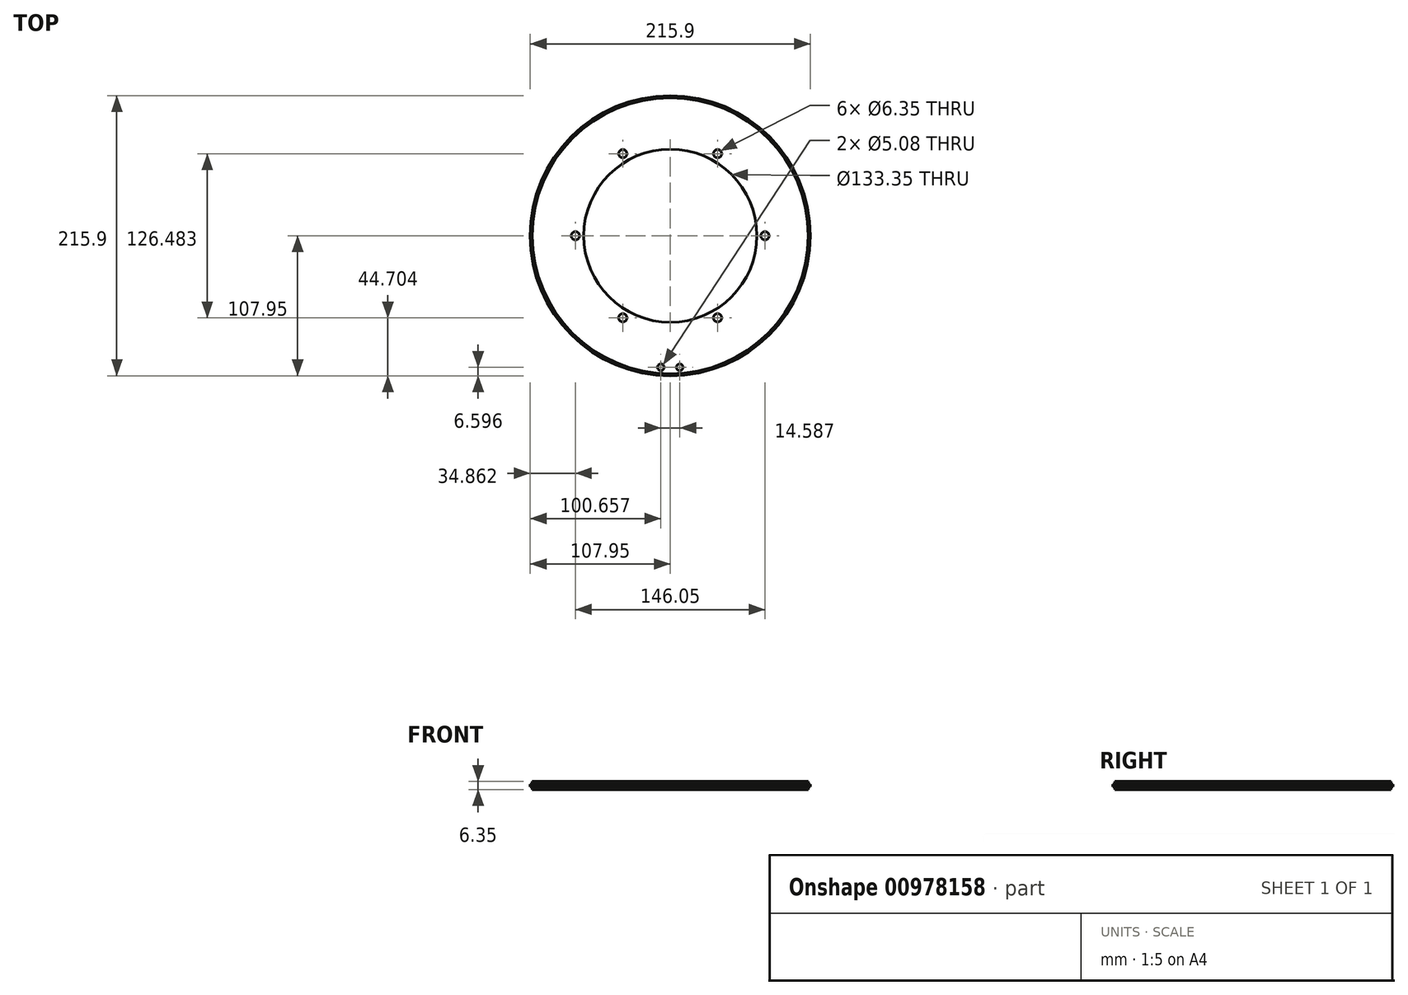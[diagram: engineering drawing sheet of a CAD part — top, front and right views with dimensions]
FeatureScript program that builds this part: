
annotation { "Feature Type Name" : "Feature", "Feature Type Description" : "" }
export const myFeature = defineFeature(function(context is Context, id is Id, definition is map)
    precondition{}
    {
        {
            var Q0;
            Q0=qCreatedBy(makeId("Top.planeOp"),FACE);
            var sketch = newSketch(context, id + "F0", { "sketchPlane" : qUnion([Q0])});
            skCircle(sketch, "E0", {"center": v(0, 0) * mm, "radius": 107.95 * mm});
            skCircle(sketch, "E1", {"center": v(0, 0) * mm, "radius": 106.35 * mm});
            skSolve(sketch);
        }
        {
            var Q0;
            Q0=makeQuery(id+"F0.imprint","IMPRINT",FACE,{"disambiguationData":[TD([[makeQuery(id+"F0.imprint","IMPRINT",EDGE,{"derivedFrom":sQuery(id+"F0.wireOp",EDGE,"E1")}),1.0]])]});
            extrude(context, id + "F1", {"entities" : qUnion([Q0]), "depth" : 2.12 * mm, "offsetDistance" : 25.4 * mm});
        }
        {
            var Q0;
            Q0=qSketchRegion(id+"F0",true);
            var Q1;
            Q1=makeQuery(id+"F1.opExtrude","CAP_FACE",FACE,{"disambiguationData":[OSD([sQuery(id+"F0.wireOp",EDGE,"E1")])],"isStart":true});
            extrude(context, id + "F2", {"entities" : qUnion([Q0, Q1]), "operationType" : NewBodyOperationType.ADD, "oppositeDirection" : true, "depth" : 2.12 * mm, "offsetDistance" : 25.4 * mm});
        }
        {
            var Q0;
            Q0=makeQuery(id+"F0.imprint","IMPRINT",FACE,{"disambiguationData":[TD([[makeQuery(id+"F0.imprint","IMPRINT",EDGE,{"derivedFrom":sQuery(id+"F0.wireOp",EDGE,"E1")}),1.0]])]});
            extrude(context, id + "F3", {"entities" : qUnion([Q0]), "operationType" : NewBodyOperationType.ADD, "oppositeDirection" : true, "depth" : 4.23 * mm, "offsetDistance" : 25.4 * mm});
        }
        {
            var Q0;
            Q0=makeQuery(id+"F1.opExtrude","CAP_FACE",FACE,{"disambiguationData":[OSD([sQuery(id+"F0.wireOp",EDGE,"E1")])],"isStart":false});
            var sketch = newSketch(context, id + "F4", { "sketchPlane" : qUnion([Q0])});
            skCircle(sketch, "E2", {"center": v(0, 0) * mm, "radius": 66.68 * mm});
            skSolve(sketch);
        }
        {
            var Q0;
            Q0=qSketchRegion(id+"F4",true);
            extrude(context, id + "F5", {"entities" : qUnion([Q0]), "operationType" : NewBodyOperationType.REMOVE, "endBound" : BoundingType.THROUGH_ALL, "oppositeDirection" : true, "depth" : 25.4 * mm, "offsetDistance" : 25.4 * mm});
        }
        {
            var Q0;
            Q0=makeQuery(id+"F1.opExtrude","CAP_FACE",FACE,{"disambiguationData":[OSD([sQuery(id+"F0.wireOp",EDGE,"E1")])],"isStart":false});
            var sketch = newSketch(context, id + "F6", { "sketchPlane" : qUnion([Q0])});
            skCircle(sketch, "E3", {"center": v(-0.06, 0) * mm, "radius": 79.4 * mm});
            skCircle(sketch, "E4", {"center": v(-0.06, 0) * mm, "radius": 77.76 * mm});
            skCircle(sketch, "E5.0", {"center": v(-73.09, 0) * mm, "radius": 3.17 * mm});
            skCircle(sketch, "E6.0", {"center": v(-36.58, 63.24) * mm, "radius": 3.17 * mm});
            skCircle(sketch, "E7.0", {"center": v(36.45, 63.24) * mm, "radius": 3.17 * mm});
            skCircle(sketch, "E8.0", {"center": v(72.96, 0) * mm, "radius": 3.17 * mm});
            skCircle(sketch, "E9.0", {"center": v(36.45, -63.25) * mm, "radius": 3.17 * mm});
            skCircle(sketch, "E10.0", {"center": v(-36.58, -63.25) * mm, "radius": 3.17 * mm});
            skCircle(sketch, "E11.0", {"center": v(-7.36, -72.66) * mm, "radius": 2.54 * mm});
            skCircle(sketch, "E12.0", {"center": v(7.23, -72.66) * mm, "radius": 2.54 * mm});
            skCircle(sketch, "E13.0", {"center": v(-0.06, 0) * mm, "radius": 66.67 * mm});
            skSolve(sketch);
        }
        {
            var Q0;
            Q0=makeQuery(id+"F6.imprint","IMPRINT",FACE,{"disambiguationData":[TD([[makeQuery(id+"F6.imprint","IMPRINT",EDGE,{"derivedFrom":sQuery(id+"F6.wireOp",EDGE,"E5.0")}),1.0]])]});
            var Q1;
            Q1=makeQuery(id+"F6.imprint","IMPRINT",FACE,{"disambiguationData":[TD([[makeQuery(id+"F6.imprint","IMPRINT",EDGE,{"derivedFrom":sQuery(id+"F6.wireOp",EDGE,"E7.0")}),1.0]])]});
            var Q2;
            Q2=makeQuery(id+"F6.imprint","IMPRINT",FACE,{"disambiguationData":[TD([[makeQuery(id+"F6.imprint","IMPRINT",EDGE,{"derivedFrom":sQuery(id+"F6.wireOp",EDGE,"E8.0")}),1.0]])]});
            var Q3;
            Q3=makeQuery(id+"F6.imprint","IMPRINT",FACE,{"disambiguationData":[TD([[makeQuery(id+"F6.imprint","IMPRINT",EDGE,{"derivedFrom":sQuery(id+"F6.wireOp",EDGE,"E9.0")}),1.0]])]});
            var Q4;
            Q4=makeQuery(id+"F6.imprint","IMPRINT",FACE,{"disambiguationData":[TD([[makeQuery(id+"F6.imprint","IMPRINT",EDGE,{"derivedFrom":sQuery(id+"F6.wireOp",EDGE,"E10.0")}),1.0]])]});
            var Q5;
            Q5=makeQuery(id+"F6.imprint","IMPRINT",FACE,{"disambiguationData":[TD([[makeQuery(id+"F6.imprint","IMPRINT",EDGE,{"derivedFrom":sQuery(id+"F6.wireOp",EDGE,"E6.0")}),1.0]])]});
            extrude(context, id + "F7", {"entities" : qUnion([Q0, Q1, Q2, Q3, Q4, Q5]), "operationType" : NewBodyOperationType.REMOVE, "oppositeDirection" : true, "depth" : 25.4 * mm, "offsetDistance" : 25.4 * mm});
        }
        {
            var Q0;
            Q0=makeQuery(id+"F1.opExtrude","CAP_FACE",FACE,{"disambiguationData":[OSD([sQuery(id+"F0.wireOp",EDGE,"E1")])],"isStart":false});
            var sketch = newSketch(context, id + "F8", { "sketchPlane" : qUnion([Q0])});
            skCircle(sketch, "E14", {"center": v(-7.3, -101.35) * mm, "radius": 2.54 * mm});
            skCircle(sketch, "E15", {"center": v(7.3, -101.35) * mm, "radius": 2.54 * mm});
            skLineSegment(sketch, "E16", {"start": v(0, 0) * mm, "end": v(0, -109.25) * mm});
            skSolve(sketch);
        }
        {
            var Q0;
            Q0=makeQuery(id+"F8.imprint","IMPRINT",FACE,{"disambiguationData":[TD([[makeQuery(id+"F8.imprint","IMPRINT",EDGE,{"derivedFrom":sQuery(id+"F8.wireOp",EDGE,"E14")}),1.0]])]});
            var Q1;
            Q1=makeQuery(id+"F8.imprint","IMPRINT",FACE,{"disambiguationData":[TD([[makeQuery(id+"F8.imprint","IMPRINT",EDGE,{"derivedFrom":sQuery(id+"F8.wireOp",EDGE,"E15")}),1.0]])]});
            extrude(context, id + "F9", {"entities" : qUnion([Q0, Q1]), "operationType" : NewBodyOperationType.REMOVE, "endBound" : BoundingType.THROUGH_ALL, "oppositeDirection" : true, "depth" : 25.4 * mm, "offsetDistance" : 25.4 * mm});
        }
    });
